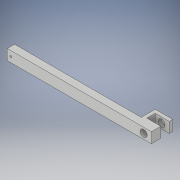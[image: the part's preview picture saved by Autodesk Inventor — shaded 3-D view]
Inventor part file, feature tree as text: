
AUTODESK INVENTOR PART (.ipt)
format: ipt  version: 2019 (Build 230136000, 136)  size: 125,440 bytes
history: native  units: in
note: dims shown in document units (in); Inventor stores cm internally (conversion verified against a paired STEP export)
features: sketch x3, hole x2, extrude x1
ambient origin geometry x8: Origin, YZ Plane, XZ Plane, XY Plane, X Axis, Y Axis, Z Axis, Center Point
bodies: Solid1 (feature_tree)
feature tree (6):
  extrude  "Extrusion1"  Depth=1.0in
  hole  "Hole1"  [1 undecoded]
  hole  "Hole2"  [1 undecoded]
  sketch  "Sketch1"  dims[d9=1.25in d10=1.0in]
  sketch  "Sketch2"  dims[d17=10.3in d24=1.525in]
  sketch  "Sketch3"  dims[d26=0.6in d27=0.25in d28=0.75in d29=0.0in d30=0.505in d31=0.75in d32=0.375in d33=0.25in d34=0.5635in d35=1.0in d36=0.8108in d37=0.55in d38=0.75in d39=0.375in d40=0.135in d41=0.75in d42=0.375in d43=0.25in d44=0.5635in d45=1.0in d46=0.8108in d47=0.75in d48=0.375in d49=0.25in d50=9.05in d51=0.25in]
note: 2 required parameter values undecoded (feature->parameter linkage not recoverable at this tier; creation-order binding heuristic only, values carry confidence <= 0.55)
